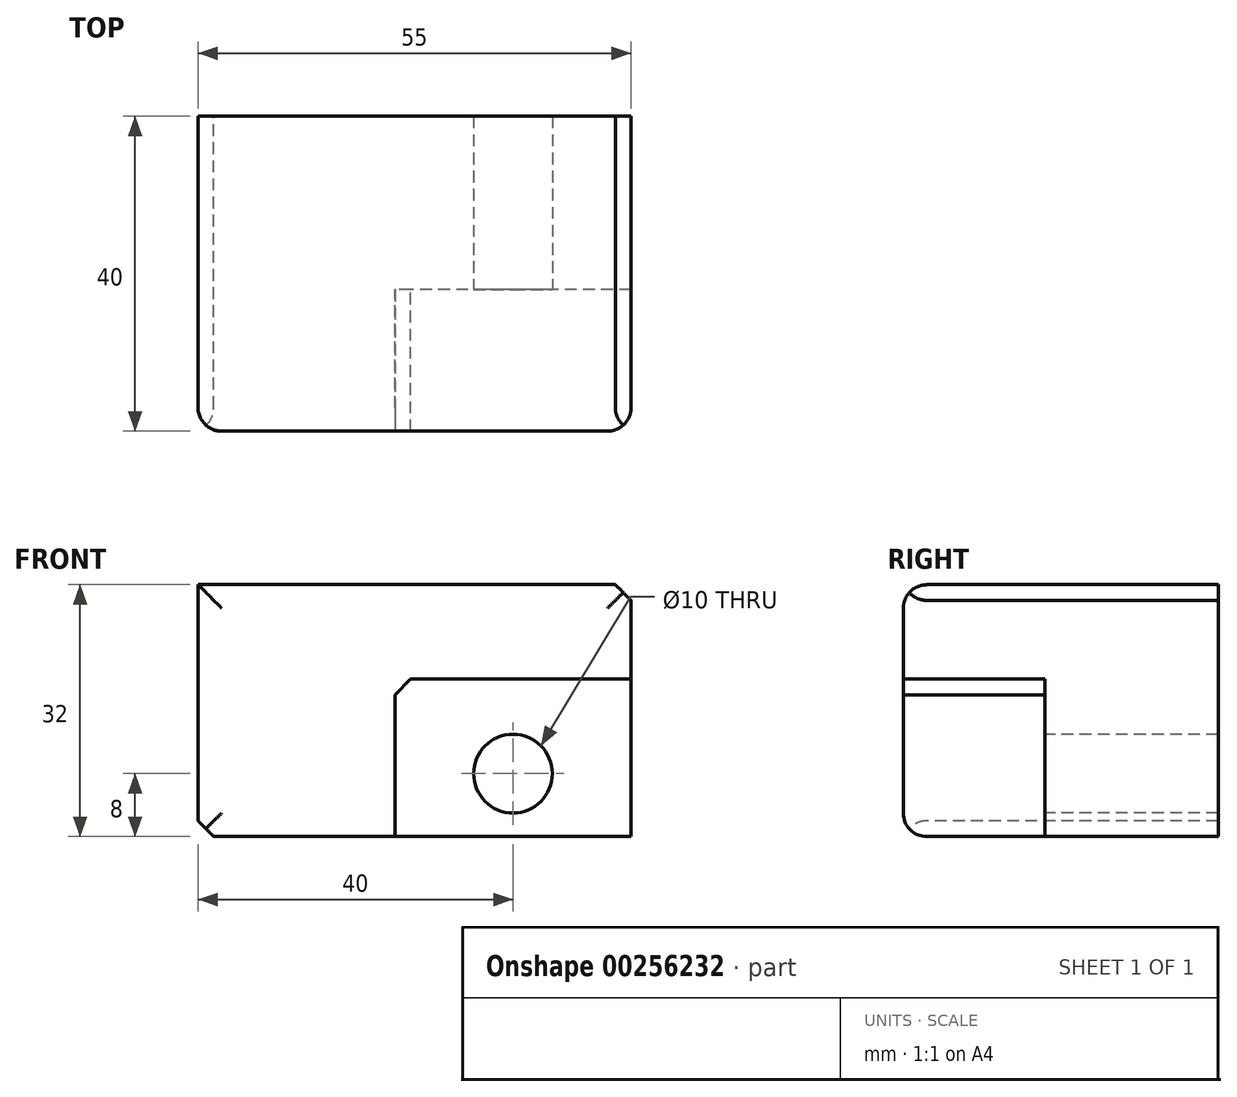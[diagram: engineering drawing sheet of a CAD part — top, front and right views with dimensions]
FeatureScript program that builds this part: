
annotation { "Feature Type Name" : "Feature", "Feature Type Description" : "" }
export const myFeature = defineFeature(function(context is Context, id is Id, definition is map)
    precondition{}
    {
        {
            var Q0;
            Q0=qCreatedBy(makeId("Front.planeOp"),FACE);
            var sketch = newSketch(context, id + "F0", { "sketchPlane" : qUnion([Q0])});
            skLineSegment(sketch, "E0.bottom", {"start": v(0, 0) * mm, "end": v(55, 0) * mm});
            skLineSegment(sketch, "E0.top", {"start": v(0, -32) * mm, "end": v(55, -32) * mm});
            skLineSegment(sketch, "E0.left", {"start": v(0, 0) * mm, "end": v(0, -32) * mm});
            skLineSegment(sketch, "E0.right", {"start": v(55, 0) * mm, "end": v(55, -32) * mm});
            skSolve(sketch);
        }
        {
            var Q0;
            Q0 = qSketchRegion(id + "F0", true);
            extrude(context, id + "F1", {"entities" : qUnion([Q0]), "depth" : 40 * mm});
        }
        {
            var Q0;
            Q0=makeQuery(id+"F1.opExtrude","SWEPT_FACE",FACE,{"disambiguationData":[OSD([sQuery(id+"F0.wireOp",EDGE,"E0.top")])]});
            var sketch = newSketch(context, id + "F2", { "sketchPlane" : qUnion([Q0])});
            skLineSegment(sketch, "E1.bottom", {"start": v(55, 40) * mm, "end": v(25, 40) * mm});
            skLineSegment(sketch, "E1.top", {"start": v(55, 22) * mm, "end": v(25, 22) * mm});
            skLineSegment(sketch, "E1.left", {"start": v(55, 40) * mm, "end": v(55, 22) * mm});
            skLineSegment(sketch, "E1.right", {"start": v(25, 40) * mm, "end": v(25, 22) * mm});
            skSolve(sketch);
        }
        {
            var Q0;
            Q0 = qSketchRegion(id + "F2", true);
            extrude(context, id + "F3", {"entities" : qUnion([Q0]), "operationType" : NewBodyOperationType.REMOVE, "oppositeDirection" : true, "depth" : 20 * mm});
        }
        {
            var Q0;
            Q0=makeQuery(id+"F3.boolean.opBoolean","COPY",FACE,{"derivedFrom":makeQuery(id+"F3.opExtrude","SWEPT_FACE",FACE,{"disambiguationData":[OSD([sQuery(id+"F2.wireOp",EDGE,"E1.top")])]})});
            var sketch = newSketch(context, id + "F4", { "sketchPlane" : qUnion([Q0])});
            skCircle(sketch, "E2", {"center": v(40, -24) * mm, "radius": 5 * mm});
            skSolve(sketch);
        }
        {
            var Q0;
            Q0 = qSketchRegion(id + "F4", true);
            extrude(context, id + "F5", {"entities" : qUnion([Q0]), "operationType" : NewBodyOperationType.REMOVE, "endBound" : BoundingType.THROUGH_ALL, "oppositeDirection" : true, "depth" : 25 * mm});
        }
        {
            var Q0;
            Q0=makeQuery(id+"F3.boolean.opBoolean","COPY",EDGE,{"derivedFrom":makeQuery(id+"F3.opExtrude","SWEPT_EDGE",EDGE,{"disambiguationData":[OSD([sQuery(id+"F0.wireOp",EDGE,"E0.top"),sQuery(id+"F2.wireOp",EDGE,"E1.bottom"),sQuery(id+"F2.wireOp",EDGE,"E1.right")])]})});
            var Q1;
            Q1=makeQuery(id+"F3.boolean.opBoolean","COPY",EDGE,{"derivedFrom":makeQuery(id+"F3.opExtrude","CAP_EDGE",EDGE,{"disambiguationData":[OSD([sQuery(id+"F2.wireOp",EDGE,"E1.right")])],"isStart":true})});
            var Q2;
            Q2=makeQuery(id+"F3.boolean.opBoolean","COPY",EDGE,{"derivedFrom":makeQuery(id+"F3.opExtrude","CAP_EDGE",EDGE,{"disambiguationData":[OSD([sQuery(id+"F2.wireOp",EDGE,"E1.right")])],"isStart":false})});
            var Q3;
            Q3=makeQuery(id+"F3.boolean.opBoolean","COPY",EDGE,{"derivedFrom":makeQuery(id+"F3.opExtrude","CAP_EDGE",EDGE,{"disambiguationData":[OSD([sQuery(id+"F2.wireOp",EDGE,"E1.left")])],"isStart":false})});
            var Q4;
            Q4=makeQuery(id+"F3.boolean.opBoolean","COPY",EDGE,{"derivedFrom":makeQuery(id+"F3.opExtrude","CAP_EDGE",EDGE,{"disambiguationData":[OSD([sQuery(id+"F2.wireOp",EDGE,"E1.bottom")])],"isStart":false})});
            var Q5;
            Q5=makeQuery(id+"F1.opExtrude","SWEPT_EDGE",EDGE,{"disambiguationData":[OSD([sQuery(id+"F0.wireOp",EDGE,"E0.bottom"),sQuery(id+"F0.wireOp",EDGE,"E0.right")])]});
            var Q6;
            Q6=makeQuery(id+"F1.opExtrude","SWEPT_EDGE",EDGE,{"disambiguationData":[OSD([sQuery(id+"F0.wireOp",EDGE,"E0.top"),sQuery(id+"F0.wireOp",EDGE,"E0.left")])]});
            chamfer(context, id + "F6", {"entities" : qUnion([Q0, Q1, Q2, Q3, Q4, Q5, Q6]), "width" : 2 * mm, "tangentPropagation" : true});
        }
        {
            var Q0;
            Q0=makeQuery(id+"F1.opExtrude","CAP_EDGE",EDGE,{"disambiguationData":[OSD([sQuery(id+"F0.wireOp",EDGE,"E0.top")])],"isStart":false});
            var Q1;
            Q1=makeQuery(id+"F1.opExtrude","CAP_EDGE",EDGE,{"disambiguationData":[OSD([sQuery(id+"F0.wireOp",EDGE,"E0.left")])],"isStart":false});
            var Q2;
            Q2=makeQuery(id+"F1.opExtrude","CAP_EDGE",EDGE,{"disambiguationData":[OSD([sQuery(id+"F0.wireOp",EDGE,"E0.bottom")])],"isStart":false});
            var Q3;
            Q3=makeQuery(id+"F1.opExtrude","CAP_EDGE",EDGE,{"disambiguationData":[OSD([sQuery(id+"F0.wireOp",EDGE,"E0.right")])],"isStart":false});
            var Q4;
            Q4=makeQuery(id+"F6.opChamfer","BLEND_EDGE",EDGE,{"blendedFrom":[makeQuery(id+"F3.boolean.opBoolean","COPY",EDGE,{"derivedFrom":makeQuery(id+"F3.opExtrude","CAP_EDGE",EDGE,{"disambiguationData":[OSD([sQuery(id+"F2.wireOp",EDGE,"E1.bottom")])],"isStart":false})}),makeQuery(id+"F1.opExtrude","CAP_FACE",FACE,{"disambiguationData":[OSD([sQuery(id+"F0.wireOp",EDGE,"E0.bottom"),sQuery(id+"F0.wireOp",EDGE,"E0.top"),sQuery(id+"F0.wireOp",EDGE,"E0.left"),sQuery(id+"F0.wireOp",EDGE,"E0.right")])],"isStart":false})],"blendedInto":[makeQuery(id+"F1.opExtrude","CAP_FACE",FACE,{"disambiguationData":[OSD([sQuery(id+"F0.wireOp",EDGE,"E0.bottom"),sQuery(id+"F0.wireOp",EDGE,"E0.top"),sQuery(id+"F0.wireOp",EDGE,"E0.left"),sQuery(id+"F0.wireOp",EDGE,"E0.right")])],"isStart":false})]});
            var Q5;
            {var subQ0=sQuery(id+"F0.wireOp",EDGE,"E0.top");Q5=makeQuery(id+"F6.opChamfer","BLEND_EDGE",EDGE,{"blendedFrom":[makeQuery(id+"F3.boolean.opBoolean","COPY",VERTEX,{"derivedFrom":makeQuery(id+"F3.opExtrude","CAP_VERTEX",VERTEX,{"disambiguationData":[OSD([subQ0,sQuery(id+"F2.wireOp",EDGE,"E1.bottom"),sQuery(id+"F2.wireOp",EDGE,"E1.right")])],"isStart":false})}),makeQuery(id+"F1.opExtrude","CAP_FACE",FACE,{"disambiguationData":[OSD([sQuery(id+"F0.wireOp",EDGE,"E0.bottom"),subQ0,sQuery(id+"F0.wireOp",EDGE,"E0.left"),sQuery(id+"F0.wireOp",EDGE,"E0.right")])],"isStart":false})],"blendedInto":[makeQuery(id+"F1.opExtrude","CAP_FACE",FACE,{"disambiguationData":[OSD([sQuery(id+"F0.wireOp",EDGE,"E0.bottom"),subQ0,sQuery(id+"F0.wireOp",EDGE,"E0.left"),sQuery(id+"F0.wireOp",EDGE,"E0.right")])],"isStart":false})]});}
            var Q6;
            {var subQ0=sQuery(id+"F0.wireOp",EDGE,"E0.top");Q6=makeQuery(id+"F6.opChamfer","BLEND_EDGE",EDGE,{"blendedFrom":[makeQuery(id+"F3.boolean.opBoolean","COPY",EDGE,{"derivedFrom":makeQuery(id+"F3.opExtrude","SWEPT_EDGE",EDGE,{"disambiguationData":[OSD([subQ0,sQuery(id+"F2.wireOp",EDGE,"E1.bottom"),sQuery(id+"F2.wireOp",EDGE,"E1.right")])]})}),makeQuery(id+"F1.opExtrude","CAP_FACE",FACE,{"disambiguationData":[OSD([sQuery(id+"F0.wireOp",EDGE,"E0.bottom"),subQ0,sQuery(id+"F0.wireOp",EDGE,"E0.left"),sQuery(id+"F0.wireOp",EDGE,"E0.right")])],"isStart":false})],"blendedInto":[makeQuery(id+"F1.opExtrude","CAP_FACE",FACE,{"disambiguationData":[OSD([sQuery(id+"F0.wireOp",EDGE,"E0.bottom"),subQ0,sQuery(id+"F0.wireOp",EDGE,"E0.left"),sQuery(id+"F0.wireOp",EDGE,"E0.right")])],"isStart":false})]});}
            fillet(context, id + "F7", {"entities" : qUnion([Q0, Q1, Q2, Q3, Q4, Q5, Q6]), "radius" : 3 * mm, "tangentPropagation" : true, "allowEdgeOverflow" : false});
        }
    });
